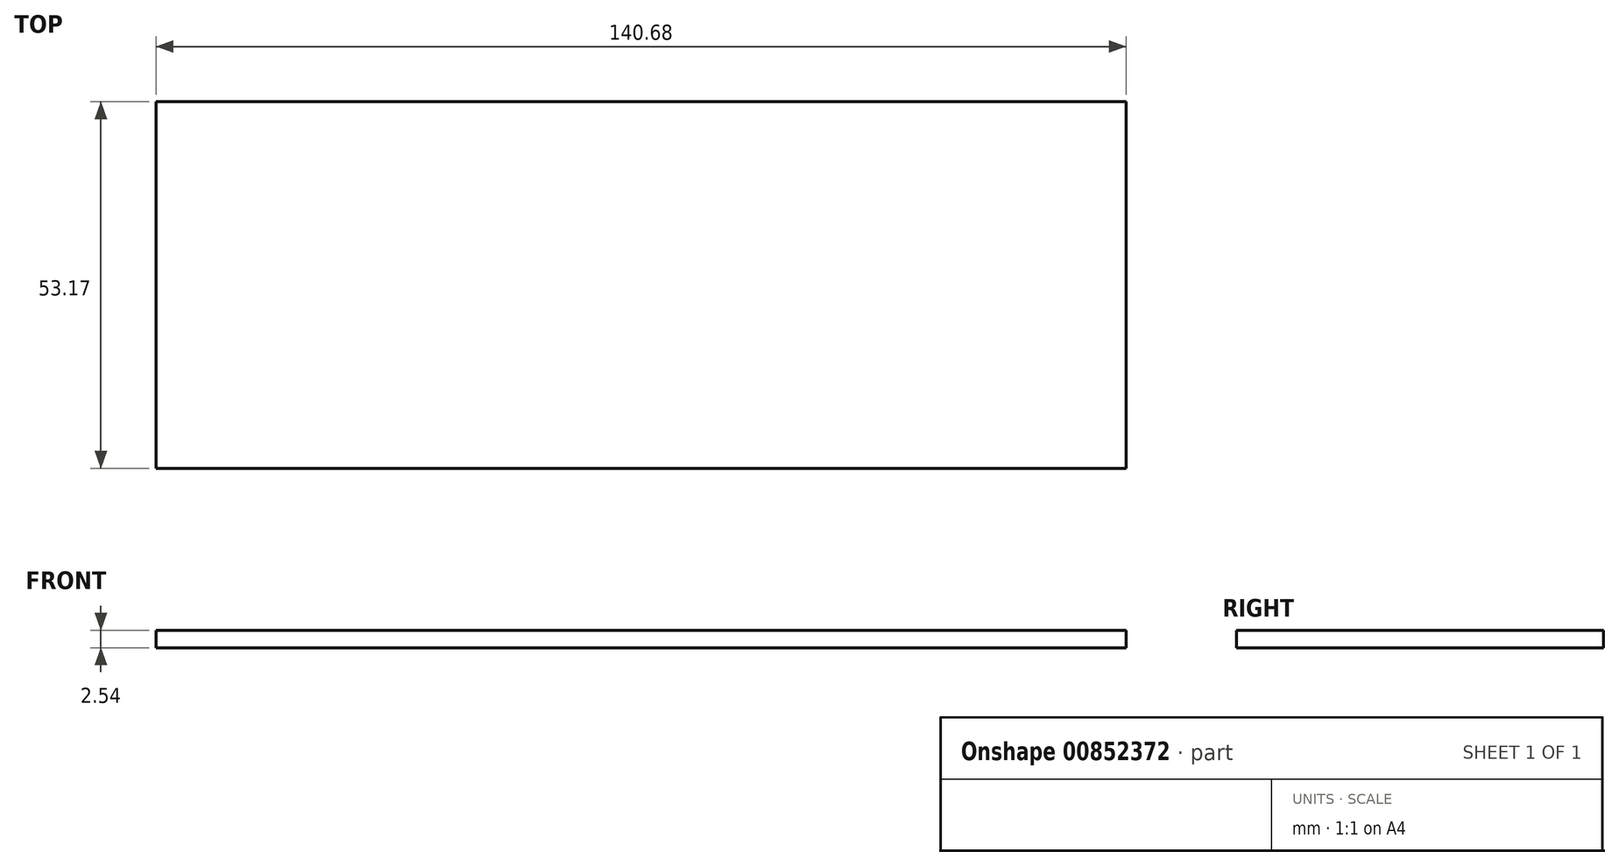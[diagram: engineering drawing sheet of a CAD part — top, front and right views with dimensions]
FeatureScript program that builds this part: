
annotation { "Feature Type Name" : "Feature", "Feature Type Description" : "" }
export const myFeature = defineFeature(function(context is Context, id is Id, definition is map)
    precondition{}
    {
        {
            var Q0;
            Q0=qCreatedBy(makeId("Top.planeOp"),FACE);
            var sketch = newSketch(context, id + "F0", { "sketchPlane" : qUnion([Q0])});
            skLineSegment(sketch, "E0.bottom", {"start": v(-70.85, 60.8) * mm, "end": v(69.83, 60.8) * mm});
            skLineSegment(sketch, "E0.top", {"start": v(-70.85, 7.63) * mm, "end": v(69.83, 7.63) * mm});
            skLineSegment(sketch, "E0.left", {"start": v(-70.85, 60.8) * mm, "end": v(-70.85, 7.63) * mm});
            skLineSegment(sketch, "E0.right", {"start": v(69.83, 60.8) * mm, "end": v(69.83, 7.63) * mm});
            skSolve(sketch);
        }
        {
            var Q0;
            Q0 = qSketchRegion(id + "F0", true);
            extrude(context, id + "F1", {"entities" : qUnion([Q0]), "depth" : 2.54 * mm, "offsetDistance" : 25.4 * mm});
        }
    });
